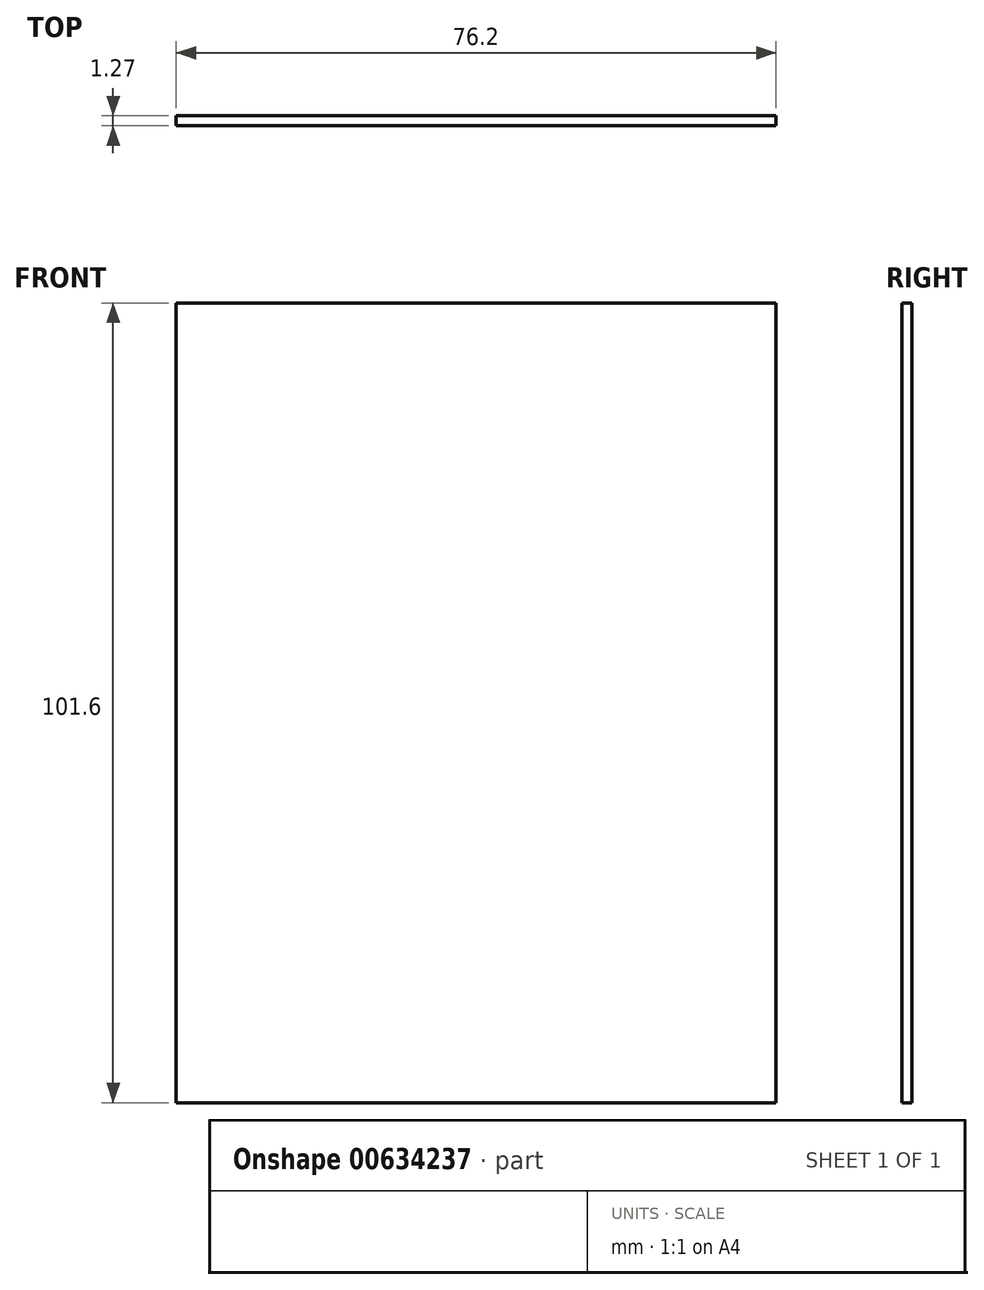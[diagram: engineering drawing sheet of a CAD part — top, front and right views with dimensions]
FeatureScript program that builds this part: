
annotation { "Feature Type Name" : "Feature", "Feature Type Description" : "" }
export const myFeature = defineFeature(function(context is Context, id is Id, definition is map)
    precondition{}
    {
        {
            var Q0;
            Q0=qCreatedBy(makeId("Front.planeOp"),FACE);
            var sketch = newSketch(context, id + "F0", { "sketchPlane" : qUnion([Q0])});
            skLineSegment(sketch, "E0.bottom", {"start": v(-65.52, 64.45) * mm, "end": v(10.68, 64.45) * mm});
            skLineSegment(sketch, "E0.top", {"start": v(-65.52, -37.15) * mm, "end": v(10.68, -37.15) * mm});
            skLineSegment(sketch, "E0.left", {"start": v(-65.52, 64.45) * mm, "end": v(-65.52, -37.15) * mm});
            skLineSegment(sketch, "E0.right", {"start": v(10.68, 64.45) * mm, "end": v(10.68, -37.15) * mm});
            skSolve(sketch);
        }
        {
            var Q0;
            Q0 = qSketchRegion(id + "F0", true);
            extrude(context, id + "F1", {"entities" : qUnion([Q0]), "oppositeDirection" : true, "depth" : 1.27 * mm, "offsetDistance" : 25.4 * mm});
        }
    });
